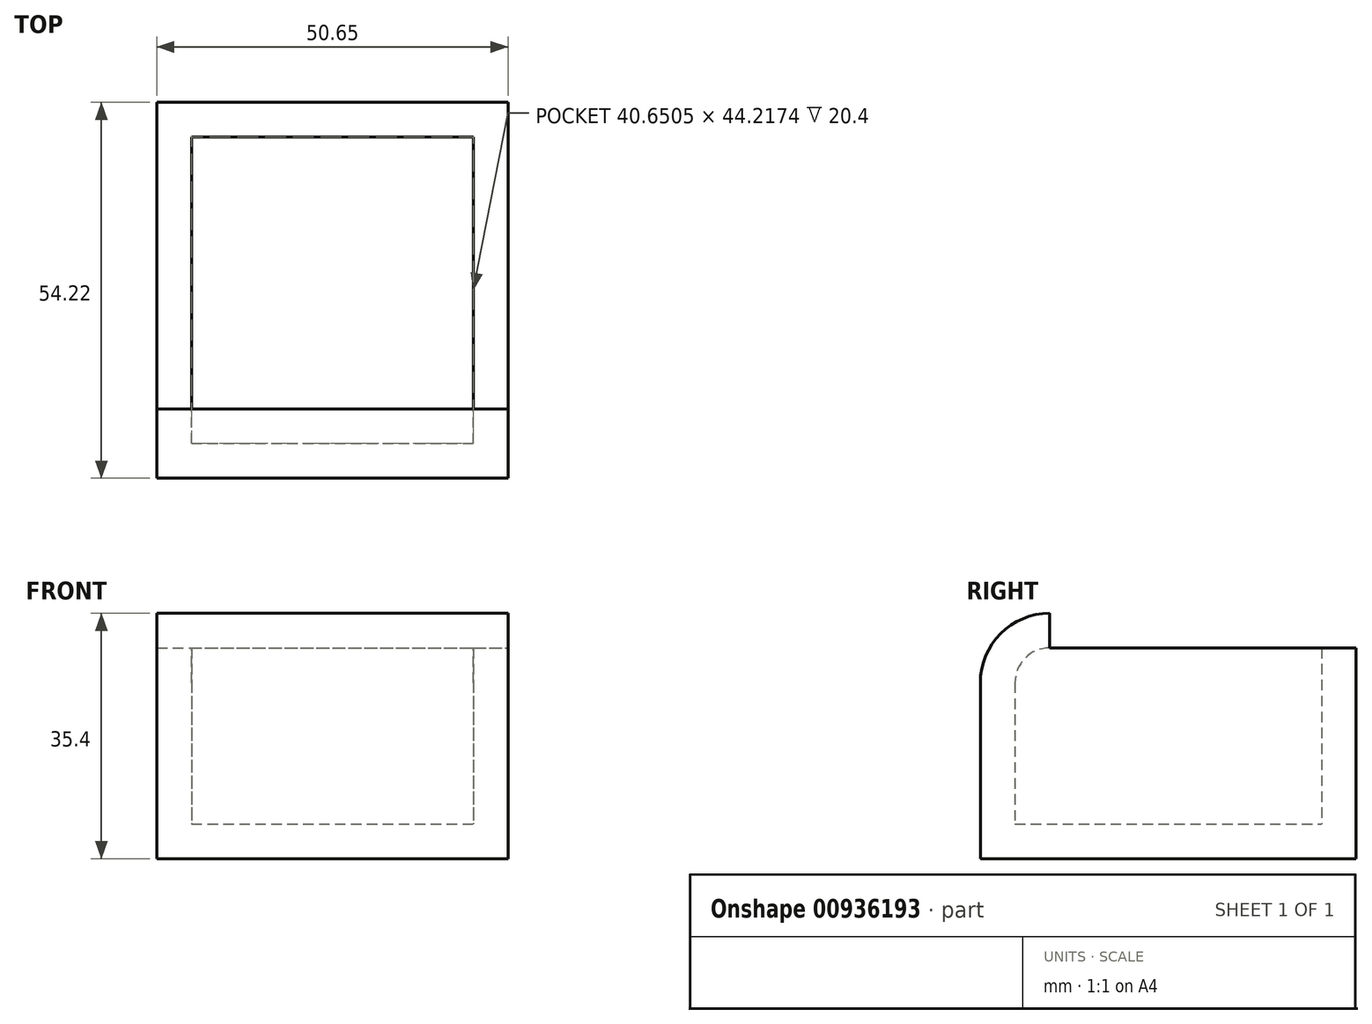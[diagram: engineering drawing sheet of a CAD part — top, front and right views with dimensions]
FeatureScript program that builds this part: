
annotation { "Feature Type Name" : "Feature", "Feature Type Description" : "" }
export const myFeature = defineFeature(function(context is Context, id is Id, definition is map)
    precondition{}
    {
        {
            var Q0;
            Q0=qCreatedBy(makeId("Top.planeOp"),FACE);
            var sketch = newSketch(context, id + "F0", { "sketchPlane" : qUnion([Q0])});
            skLineSegment(sketch, "E0.bottom", {"start": v(0, 0) * mm, "end": v(40.65, 0) * mm});
            skLineSegment(sketch, "E0.top", {"start": v(0, 44.22) * mm, "end": v(40.65, 44.22) * mm});
            skLineSegment(sketch, "E0.left", {"start": v(0, 0) * mm, "end": v(0, 44.22) * mm});
            skLineSegment(sketch, "E0.right", {"start": v(40.65, 0) * mm, "end": v(40.65, 44.22) * mm});
            skSolve(sketch);
        }
        {
            var Q0;
            Q0 = qSketchRegion(id + "F0", true);
            extrude(context, id + "F1", {"entities" : qUnion([Q0]), "depth" : 25.4 * mm, "offsetDistance" : 25.4 * mm});
        }
        {
            var Q0;
            Q0=makeQuery(id+"F1.opExtrude","CAP_EDGE",EDGE,{"disambiguationData":[OSD([sQuery(id+"F0.wireOp",EDGE,"E0.bottom")])],"isStart":false});
            fillet(context, id + "F2", {"entities" : qUnion([Q0]), "radius" : 5 * mm, "allowEdgeOverflow" : false});
        }
        {
            var Q0;
            Q0=makeQuery(id+"F1.opExtrude","CAP_FACE",FACE,{"disambiguationData":[OSD([sQuery(id+"F0.wireOp",EDGE,"E0.bottom"),sQuery(id+"F0.wireOp",EDGE,"E0.top"),sQuery(id+"F0.wireOp",EDGE,"E0.left"),sQuery(id+"F0.wireOp",EDGE,"E0.right")])],"isStart":false});
            shell(context, id + "F3", {"entities" : qUnion([Q0]), "thickness" : 5 * mm, "oppositeDirection" : true});
        }
    });
